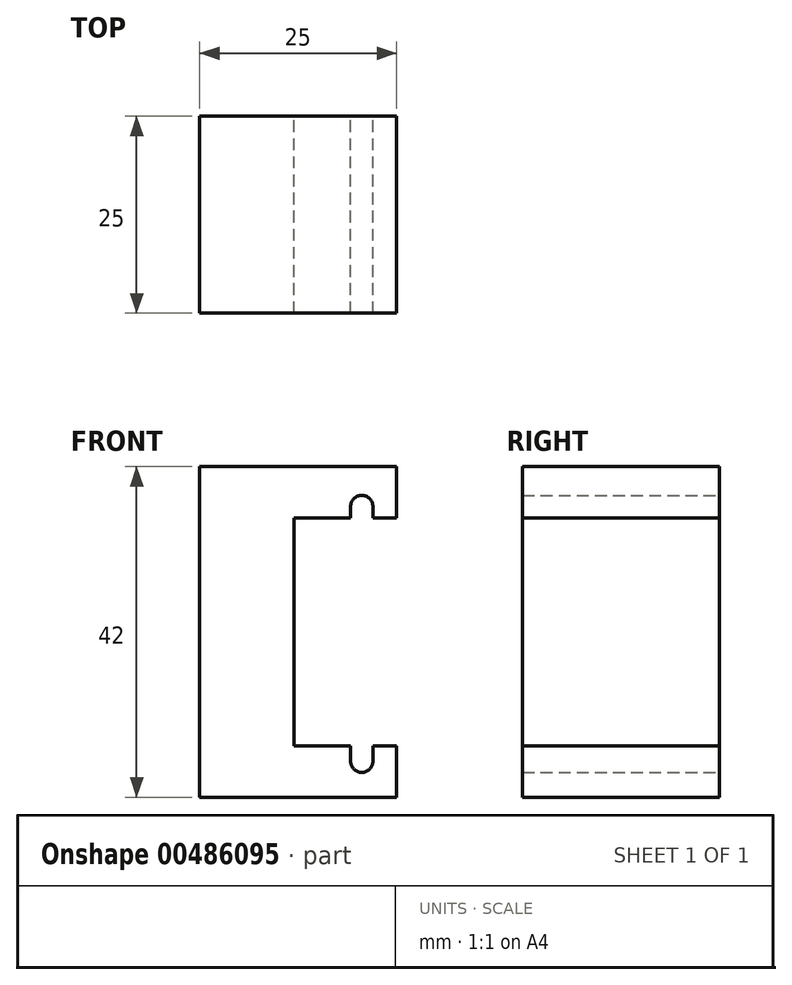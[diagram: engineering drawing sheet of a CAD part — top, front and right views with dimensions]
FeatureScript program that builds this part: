
annotation { "Feature Type Name" : "Feature", "Feature Type Description" : "" }
export const myFeature = defineFeature(function(context is Context, id is Id, definition is map)
    precondition{}
    {
        {
            var Q0;
            Q0=qCreatedBy(makeId("Front.planeOp"),FACE);
            var sketch = newSketch(context, id + "F0", { "sketchPlane" : qUnion([Q0])});
            skLineSegment(sketch, "E0.bottom", {"start": v(0, 0) * mm, "end": v(25, 0) * mm});
            skLineSegment(sketch, "E0.top", {"start": v(0, 42) * mm, "end": v(25, 42) * mm});
            skLineSegment(sketch, "E0.left", {"start": v(0, 0) * mm, "end": v(0, 42) * mm});
            skLineSegment(sketch, "E0.right", {"start": v(25, 0) * mm, "end": v(25, 6.5) * mm});
            skLineSegment(sketch, "E1.bottom", {"start": v(25, 35.5) * mm, "end": v(22, 35.5) * mm});
            skLineSegment(sketch, "E1.right", {"start": v(12, 35.5) * mm, "end": v(12, 6.5) * mm});
            skLineSegment(sketch, "E2.left", {"start": v(22, 35.5) * mm, "end": v(22, 36.92) * mm});
            skLineSegment(sketch, "E2.right", {"start": v(19.15, 35.5) * mm, "end": v(19.15, 36.92) * mm});
            skLineSegment(sketch, "E3", {"start": v(20.57, 35.5) * mm, "end": v(20.57, 36.92) * mm, "construction": true});
            skPoint(sketch, "E4", {"position": v(19.15, 36.92) * mm});
            skLineSegment(sketch, "E5", {"start": v(19.15, 36.92) * mm, "end": v(22, 36.92) * mm, "construction": true});
            skPoint(sketch, "E6", {"position": v(20.57, 36.92) * mm});
            skArc(sketch, "E7", {"start": v(19.15, 36.92) * mm, "mid": v(20.57, 38.35) * mm, "end": v(22, 36.92) * mm});
            skLineSegment(sketch, "E8.trimOffspring", {"start": v(19.15, 35.5) * mm, "end": v(12, 35.5) * mm});
            skLineSegment(sketch, "E9", {"start": v(19.15, 35.5) * mm, "end": v(22, 35.5) * mm, "construction": true});
            skLineSegment(sketch, "E10", {"start": v(22, 6.5) * mm, "end": v(22, 4.57) * mm});
            skLineSegment(sketch, "E11", {"start": v(22, 4.57) * mm, "end": v(19.15, 4.57) * mm, "construction": true});
            skLineSegment(sketch, "E12", {"start": v(19.15, 4.57) * mm, "end": v(19.15, 6.5) * mm});
            skLineSegment(sketch, "E13", {"start": v(12, 6.5) * mm, "end": v(19.15, 6.5) * mm});
            skLineSegment(sketch, "E14", {"start": v(19.15, 6.5) * mm, "end": v(22, 6.5) * mm, "construction": true});
            skLineSegment(sketch, "E15", {"start": v(22, 6.5) * mm, "end": v(25, 6.5) * mm});
            skLineSegment(sketch, "E16", {"start": v(20.57, 6.5) * mm, "end": v(20.57, 4.57) * mm, "construction": true});
            skLineSegment(sketch, "E17", {"start": v(20.57, 4.57) * mm, "end": v(20.57, 3.15) * mm, "construction": true});
            skArc(sketch, "E18", {"start": v(22, 4.57) * mm, "mid": v(20.57, 3.15) * mm, "end": v(19.15, 4.57) * mm});
            skLineSegment(sketch, "E19.trimOffspring", {"start": v(25, 35.5) * mm, "end": v(25, 42) * mm});
            skLineSegment(sketch, "E20", {"start": v(20.57, 36.92) * mm, "end": v(20.57, 38.35) * mm, "construction": true});
            skSolve(sketch);
        }
        {
            var Q0;
            Q0 = qSketchRegion(id + "F0", true);
            extrude(context, id + "F1", {"entities" : qUnion([Q0]), "depth" : 25 * mm});
        }
    });
